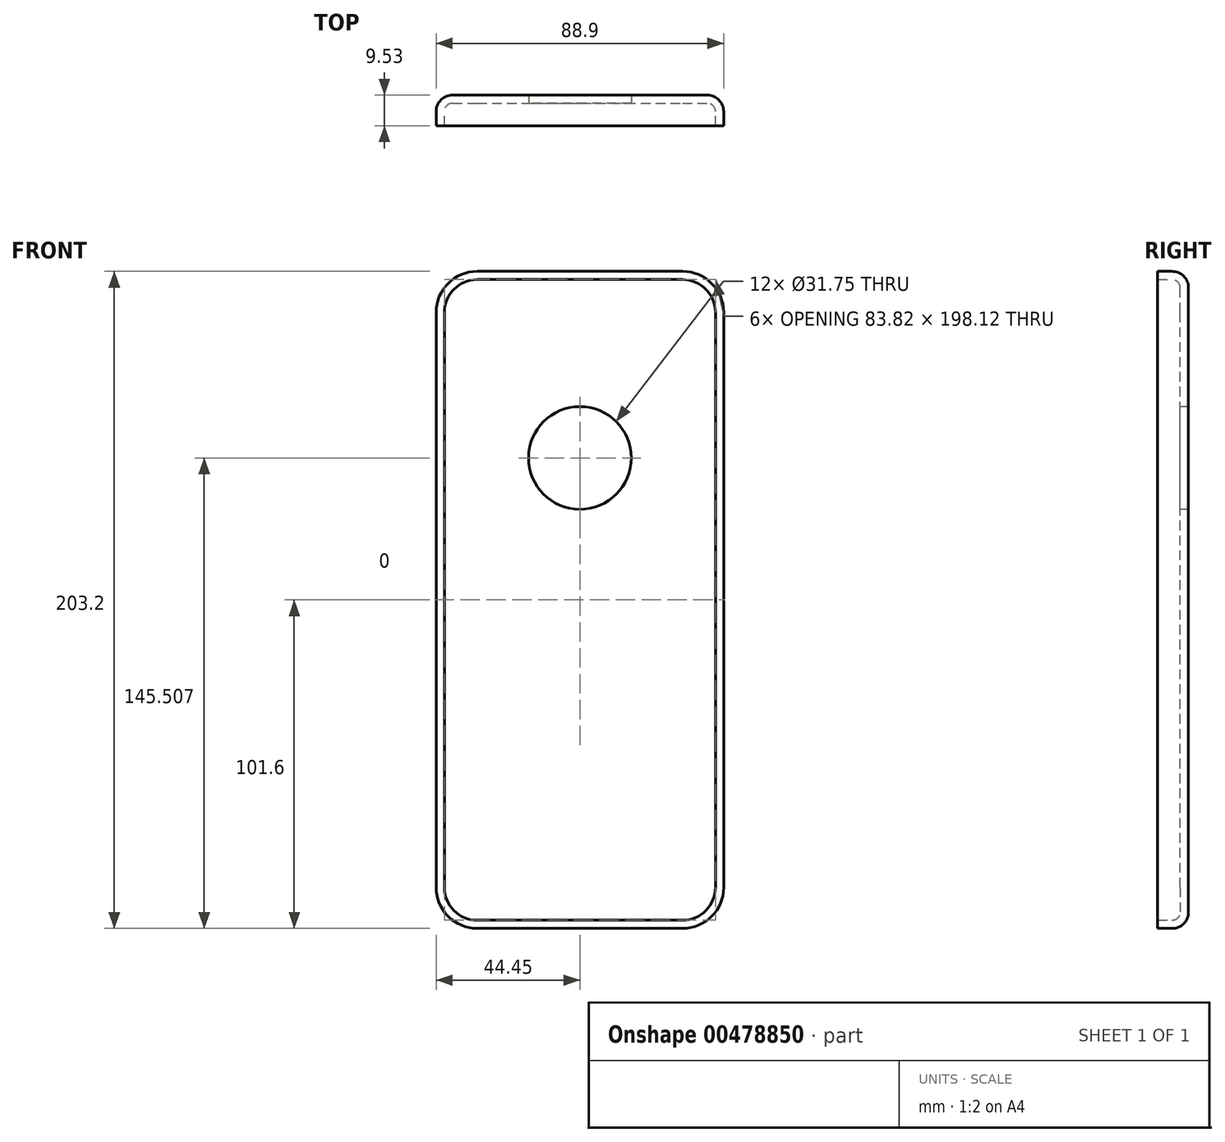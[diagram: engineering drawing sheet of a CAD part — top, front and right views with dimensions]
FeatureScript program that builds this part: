
annotation { "Feature Type Name" : "Feature", "Feature Type Description" : "" }
export const myFeature = defineFeature(function(context is Context, id is Id, definition is map)
    precondition{}
    {
        {
            var Q0;
            Q0=qCreatedBy(makeId("Front.planeOp"),FACE);
            var sketch = newSketch(context, id + "F0", { "sketchPlane" : qUnion([Q0])});
            skLineSegment(sketch, "E0.bottom", {"start": v(-31.75, 101.6) * mm, "end": v(31.75, 101.6) * mm});
            skLineSegment(sketch, "E0.top", {"start": v(-31.75, -101.6) * mm, "end": v(31.75, -101.6) * mm});
            skLineSegment(sketch, "E0.left", {"start": v(-44.45, 88.9) * mm, "end": v(-44.45, -88.9) * mm});
            skLineSegment(sketch, "E0.right", {"start": v(44.45, 88.9) * mm, "end": v(44.45, -88.9) * mm});
            skPoint(sketch, "E0.middle", {"position": v(0, 0) * mm});
            skPoint(sketch, "E1.visualSharp", {"position": v(-44.45, 101.6) * mm});
            skArc(sketch, "E1.filletArc", {"start": v(-31.75, 101.6) * mm, "mid": v(-40.73, 97.88) * mm, "end": v(-44.45, 88.9) * mm});
            skPoint(sketch, "E2.visualSharp", {"position": v(44.45, 101.6) * mm});
            skArc(sketch, "E2.filletArc", {"start": v(44.45, 88.9) * mm, "mid": v(40.73, 97.88) * mm, "end": v(31.75, 101.6) * mm});
            skPoint(sketch, "E3.visualSharp", {"position": v(44.45, -101.6) * mm});
            skArc(sketch, "E3.filletArc", {"start": v(31.75, -101.6) * mm, "mid": v(40.73, -97.88) * mm, "end": v(44.45, -88.9) * mm});
            skPoint(sketch, "E4.visualSharp", {"position": v(-44.45, -101.6) * mm});
            skArc(sketch, "E4.filletArc", {"start": v(-44.45, -88.9) * mm, "mid": v(-40.73, -97.88) * mm, "end": v(-31.75, -101.6) * mm});
            skSolve(sketch);
        }
        {
            var Q0;
            Q0=makeQuery(id+"F0.imprint","IMPRINT",FACE,{"disambiguationData":[TD([[makeQuery(id+"F0.imprint","IMPRINT",EDGE,{"derivedFrom":sQuery(id+"F0.wireOp",EDGE,"E0.bottom")}),-1.0]])]});
            extrude(context, id + "F1", {"entities" : qUnion([Q0]), "depth" : 9.52 * mm});
        }
        {
            var Q0;
            Q0=makeQuery(id+"F1.opExtrude","CAP_FACE",FACE,{"disambiguationData":[OSD([sQuery(id+"F0.wireOp",EDGE,"E0.bottom"),sQuery(id+"F0.wireOp",EDGE,"E0.top"),sQuery(id+"F0.wireOp",EDGE,"E0.left"),sQuery(id+"F0.wireOp",EDGE,"E0.right"),sQuery(id+"F0.wireOp",EDGE,"E1.filletArc"),sQuery(id+"F0.wireOp",EDGE,"E2.filletArc"),sQuery(id+"F0.wireOp",EDGE,"E3.filletArc"),sQuery(id+"F0.wireOp",EDGE,"E4.filletArc")])],"isStart":true});
            fillet(context, id + "F2", {"entities" : qUnion([Q0]), "radius" : 5.08 * mm, "tangentPropagation" : true, "allowEdgeOverflow" : false});
        }
        {
            var Q0;
            Q0=makeQuery(id+"F1.opExtrude","CAP_FACE",FACE,{"disambiguationData":[OSD([sQuery(id+"F0.wireOp",EDGE,"E0.bottom"),sQuery(id+"F0.wireOp",EDGE,"E0.top"),sQuery(id+"F0.wireOp",EDGE,"E0.left"),sQuery(id+"F0.wireOp",EDGE,"E0.right"),sQuery(id+"F0.wireOp",EDGE,"E1.filletArc"),sQuery(id+"F0.wireOp",EDGE,"E2.filletArc"),sQuery(id+"F0.wireOp",EDGE,"E3.filletArc"),sQuery(id+"F0.wireOp",EDGE,"E4.filletArc")])],"isStart":false});
            shell(context, id + "F3", {"entities" : qUnion([Q0]), "thickness" : 2.54 * mm});
        }
        {
            var Q0;
            Q0=makeQuery(id+"F3.opShell","OFFSET_FACE",FACE,{"disambiguationData":[OSD([sQuery(id+"F0.wireOp",EDGE,"E0.bottom"),sQuery(id+"F0.wireOp",EDGE,"E0.top"),sQuery(id+"F0.wireOp",EDGE,"E0.left"),sQuery(id+"F0.wireOp",EDGE,"E0.right"),sQuery(id+"F0.wireOp",EDGE,"E1.filletArc"),sQuery(id+"F0.wireOp",EDGE,"E2.filletArc"),sQuery(id+"F0.wireOp",EDGE,"E3.filletArc"),sQuery(id+"F0.wireOp",EDGE,"E4.filletArc")])]});
            var sketch = newSketch(context, id + "F4", { "sketchPlane" : qUnion([Q0])});
            skCircle(sketch, "E5", {"center": v(0, 43.9) * mm, "radius": 15.88 * mm});
            skSolve(sketch);
        }
        {
            var Q0;
            Q0 = qSketchRegion(id + "F4", true);
            extrude(context, id + "F5", {"entities" : qUnion([Q0]), "operationType" : NewBodyOperationType.REMOVE, "oppositeDirection" : true, "depth" : 25.4 * mm});
        }
    });
